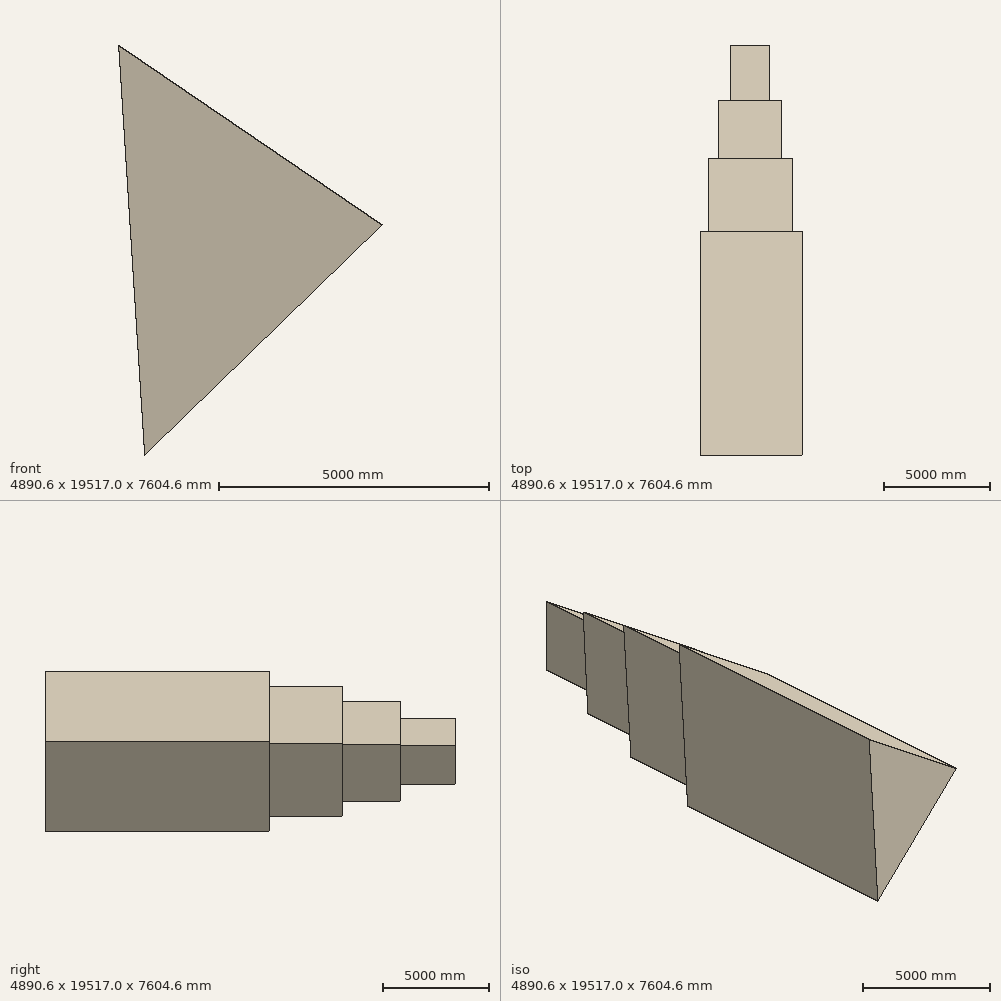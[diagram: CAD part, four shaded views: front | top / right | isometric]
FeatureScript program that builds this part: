
annotation { "Feature Type Name" : "Feature", "Feature Type Description" : "" }
export const myFeature = defineFeature(function(context is Context, id is Id, definition is map)
    precondition{}
    {
        {
            var Q0;
            Q0=qCreatedBy(makeId("Front.planeOp"),FACE);
            var sketch = newSketch(context, id + "F0", { "sketchPlane" : qUnion([Q0])});
            skLineSegment(sketch, "E0", {"start": v(483.69, 0) * mm, "end": v(5954.6, 5304.11) * mm});
            skLineSegment(sketch, "E1", {"start": v(6297.32, 3314.15) * mm, "end": v(0, 7604.63) * mm});
            skLineSegment(sketch, "E2", {"start": v(0, 7604.63) * mm, "end": v(483.69, 0) * mm});
            skSolve(sketch);
        }
        {
            var Q0;
            {var subQ0=sQuery(id+"F0.wireOp",EDGE,"E2");Q0=makeQuery(id+"F0.imprint","IMPRINT",FACE,{"disambiguationData":[TD([[makeQuery(id+"F0.imprint","IMPRINT",EDGE,{"derivedFrom":subQ0}),1.0]])]});}
            extrude(context, id + "F1", {"entities" : qUnion([Q0]), "depth" : 10657.73 * mm});
        }
        {
            var Q0;
            Q0=makeQuery(id+"F1.opExtrude","SWEPT_FACE",FACE,{"disambiguationData":[OSD([sQuery(id+"F0.wireOp",EDGE,"E2")])]});
            var sketch = newSketch(context, id + "F2", { "sketchPlane" : qUnion([Q0])});
            skLineSegment(sketch, "E3", {"start": v(169.5, 7435.59) * mm, "end": v(10517.16, 7435.59) * mm});
            skLineSegment(sketch, "E4", {"start": v(10517.16, 182.1) * mm, "end": v(10517.16, 7435.59) * mm});
            skLineSegment(sketch, "E5", {"start": v(10517.16, 182.1) * mm, "end": v(244.58, 182.1) * mm});
            skLineSegment(sketch, "E6", {"start": v(244.58, 182.1) * mm, "end": v(169.5, 7435.59) * mm});
            skSolve(sketch);
        }
        {
            var Q0;
            Q0=sQuery(id+"F2.wireOp",VERTEX,"E3.start");
            var Q1;
            Q1=sQuery(id+"F2.wireOp",VERTEX,"E6.start");
            var Q2;
            Q2=sQuery(id+"F2.wireOp",VERTEX,"E5.start");
            var Q3;
            Q3=sQuery(id+"F2.wireOp",VERTEX,"E4.end");
            var Q4;
            Q4=makeQuery(id+"F1.opExtrude","SWEPT_BODY",BODY,{"disambiguationData":[OSD([sQuery(id+"F0.wireOp",EDGE,"E0"),sQuery(id+"F0.wireOp",EDGE,"E1"),sQuery(id+"F0.wireOp",EDGE,"E2")])]});
            hole(context, id + "F3", {"style" : HoleStyle.SIMPLE, "holeDiameter" : 6.35 * mm, "endStyle" : HoleEndStyle.THROUGH, "locations" : qUnion([Q0, Q1, Q2, Q3]), "scope" : qUnion([Q4])});
        }
        {
            var Q0;
            Q0=makeQuery(id+"F1.opExtrude","CAP_FACE",FACE,{"disambiguationData":[OSD([sQuery(id+"F0.wireOp",EDGE,"E0"),sQuery(id+"F0.wireOp",EDGE,"E1"),sQuery(id+"F0.wireOp",EDGE,"E2")])],"isStart":true});
            var sketch = newSketch(context, id + "F4", { "sketchPlane" : qUnion([Q0])});
            skLineSegment(sketch, "E7", {"start": v(-390.74, 6892.01) * mm, "end": v(-4392.3, 4165.67) * mm});
            skLineSegment(sketch, "E8", {"start": v(-4392.3, 4165.67) * mm, "end": v(-788.22, 671.46) * mm});
            skLineSegment(sketch, "E9", {"start": v(-804.44, 654.73) * mm, "end": v(-390.74, 6892.01) * mm});
            skSolve(sketch);
        }
        {
            var Q0;
            {var subQ0=sQuery(id+"F4.wireOp",EDGE,"E7");Q0=makeQuery(id+"F4.imprint","IMPRINT",FACE,{"disambiguationData":[TD([[makeQuery(id+"F4.imprint","IMPRINT",EDGE,{"derivedFrom":subQ0}),1.0]])]});}
            extrude(context, id + "F5", {"entities" : qUnion([Q0]), "operationType" : NewBodyOperationType.ADD, "depth" : 3494.1 * mm});
        }
        {
            var Q0;
            Q0=makeQuery(id+"F5.opExtrude","CAP_FACE",FACE,{"disambiguationData":[OSD([sQuery(id+"F4.wireOp",EDGE,"E7"),sQuery(id+"F4.wireOp",EDGE,"E8"),sQuery(id+"F4.wireOp",EDGE,"E9")])],"isStart":false});
            var sketch = newSketch(context, id + "F6", { "sketchPlane" : qUnion([Q0])});
            skLineSegment(sketch, "E10", {"start": v(-3854.69, 4150.5) * mm, "end": v(-801.3, 6230.84) * mm});
            skLineSegment(sketch, "E11", {"start": v(-847.43, 6298.55) * mm, "end": v(-1117.92, 1445.56) * mm});
            skLineSegment(sketch, "E12", {"start": v(-1117.92, 1445.56) * mm, "end": v(-3854.69, 4150.5) * mm});
            skSolve(sketch);
        }
        {
            var Q0;
            {var subQ0=sQuery(id+"F6.wireOp",EDGE,"E12");Q0=makeQuery(id+"F6.imprint","IMPRINT",FACE,{"disambiguationData":[TD([[makeQuery(id+"F6.imprint","IMPRINT",EDGE,{"derivedFrom":subQ0}),-1.0]])]});}
            extrude(context, id + "F7", {"entities" : qUnion([Q0]), "operationType" : NewBodyOperationType.ADD, "depth" : 2730.34 * mm});
        }
        {
            var Q0;
            Q0=makeQuery(id+"F7.opExtrude","CAP_FACE",FACE,{"disambiguationData":[OSD([sQuery(id+"F6.wireOp",EDGE,"E10"),sQuery(id+"F6.wireOp",EDGE,"E11"),sQuery(id+"F6.wireOp",EDGE,"E12")])],"isStart":false});
            var sketch = newSketch(context, id + "F8", { "sketchPlane" : qUnion([Q0])});
            skLineSegment(sketch, "E13", {"start": v(-3305.74, 4078.9) * mm, "end": v(-1438.05, 5351.4) * mm});
            skLineSegment(sketch, "E14", {"start": v(-1438.05, 5351.4) * mm, "end": v(-1438.05, 2233.18) * mm});
            skLineSegment(sketch, "E15", {"start": v(-1438.05, 2233.18) * mm, "end": v(-3305.74, 4078.9) * mm});
            skSolve(sketch);
        }
        {
            var Q0;
            Q0=makeQuery(id+"F8.imprint","IMPRINT",FACE,{"disambiguationData":[TD([[makeQuery(id+"F8.imprint","IMPRINT",EDGE,{"derivedFrom":sQuery(id+"F8.wireOp",EDGE,"E13")}),-1.0]])]});
            extrude(context, id + "F9", {"entities" : qUnion([Q0]), "operationType" : NewBodyOperationType.ADD, "depth" : 2634.88 * mm});
        }
    });
